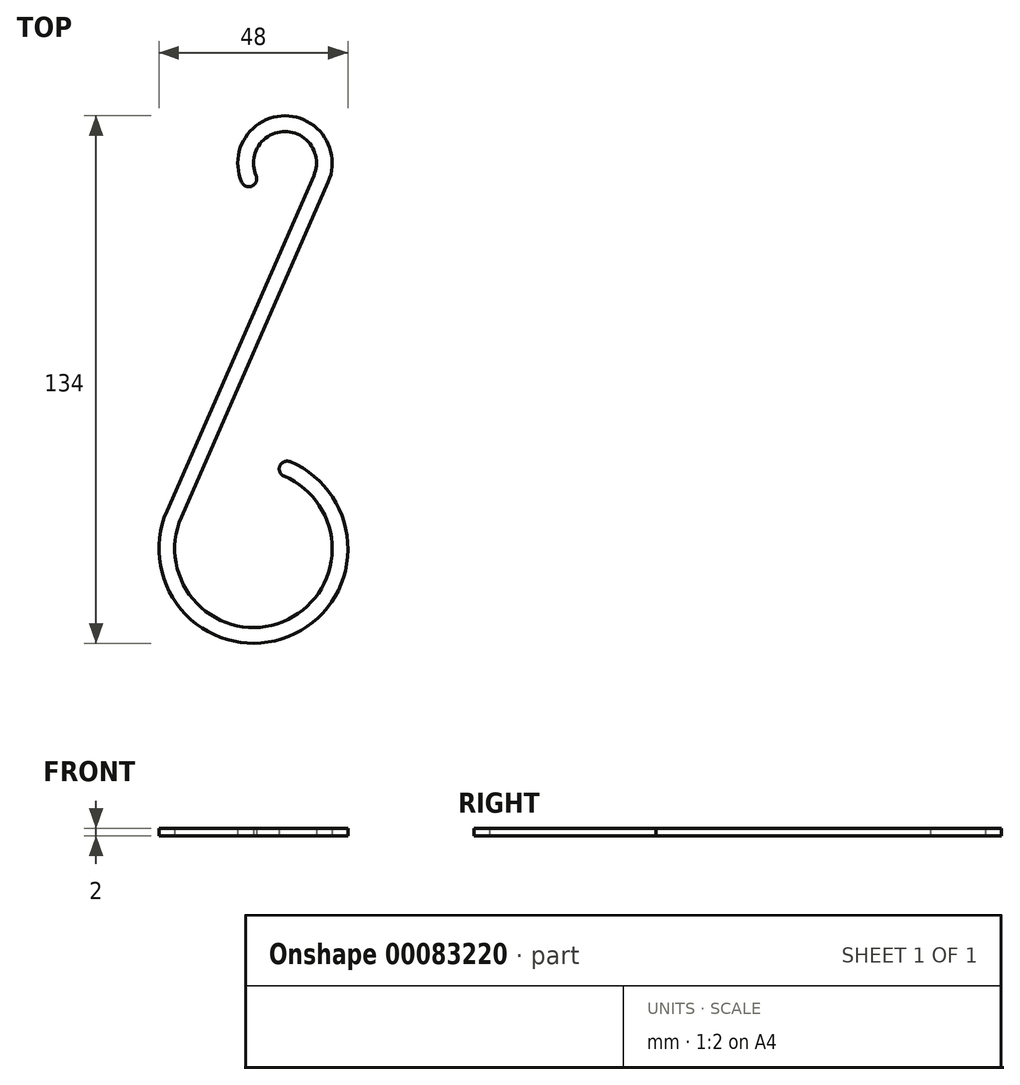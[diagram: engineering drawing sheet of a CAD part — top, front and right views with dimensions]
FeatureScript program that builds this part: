
annotation { "Feature Type Name" : "Feature", "Feature Type Description" : "" }
export const myFeature = defineFeature(function(context is Context, id is Id, definition is map)
    precondition{}
    {
        {
            var Q0;
            Q0=qCreatedBy(makeId("Top.planeOp"),FACE);
            var sketch = newSketch(context, id + "F0", { "sketchPlane" : qUnion([Q0])});
            skLineSegment(sketch, "E0.bottom", {"start": v(-25, 65) * mm, "end": v(25, 65) * mm, "construction": true});
            skLineSegment(sketch, "E0.top", {"start": v(-25, -65) * mm, "end": v(25, -65) * mm, "construction": true});
            skLineSegment(sketch, "E0.left", {"start": v(-25, 65) * mm, "end": v(-25, -65) * mm, "construction": true});
            skLineSegment(sketch, "E0.right", {"start": v(25, 65) * mm, "end": v(25, -65) * mm, "construction": true});
            skPoint(sketch, "E0.middle", {"position": v(0, 0) * mm});
            skCircle(sketch, "E1", {"center": v(5, -45) * mm, "radius": 20 * mm, "construction": true});
            skCircle(sketch, "E2", {"center": v(13, 53) * mm, "radius": 12 * mm, "construction": true});
            skLineSegment(sketch, "E3", {"start": v(24, 48.18) * mm, "end": v(-13.32, -36.97) * mm});
            skArc(sketch, "E4", {"start": v(-13.32, -36.97) * mm, "mid": v(12.4, -63.58) * mm, "end": v(12.77, -26.57) * mm});
            skArc(sketch, "E5", {"start": v(24, 48.18) * mm, "mid": v(13, 65) * mm, "end": v(2, 48.18) * mm});
            skArc(sketch, "E6.0", {"start": v(20.33, 49.79) * mm, "mid": v(13, 61) * mm, "end": v(5.67, 49.79) * mm});
            skLineSegment(sketch, "E6.1", {"start": v(20.33, 49.79) * mm, "end": v(-16.98, -35.37) * mm});
            skArc(sketch, "E6.2", {"start": v(-16.98, -35.37) * mm, "mid": v(13.89, -67.3) * mm, "end": v(14.33, -22.89) * mm});
            skLineSegment(sketch, "E7", {"start": v(14.33, -22.89) * mm, "end": v(12.77, -26.57) * mm, "construction": true});
            skArc(sketch, "E8", {"start": v(14.33, -22.89) * mm, "mid": v(11.7, -23.95) * mm, "end": v(12.77, -26.57) * mm});
            skArc(sketch, "E9", {"start": v(2, 48.18) * mm, "mid": v(4.64, 47.16) * mm, "end": v(5.67, 49.79) * mm});
            skSolve(sketch);
        }
        {
            var Q0;
            Q0=makeQuery(id+"F0.imprint","IMPRINT",FACE,{"disambiguationData":[TD([[makeQuery(id+"F0.imprint","IMPRINT",EDGE,{"derivedFrom":sQuery(id+"F0.wireOp",EDGE,"E3")}),-1.0]])]});
            extrude(context, id + "F1", {"entities" : qUnion([Q0]), "depth" : 2 * mm});
        }
    });
